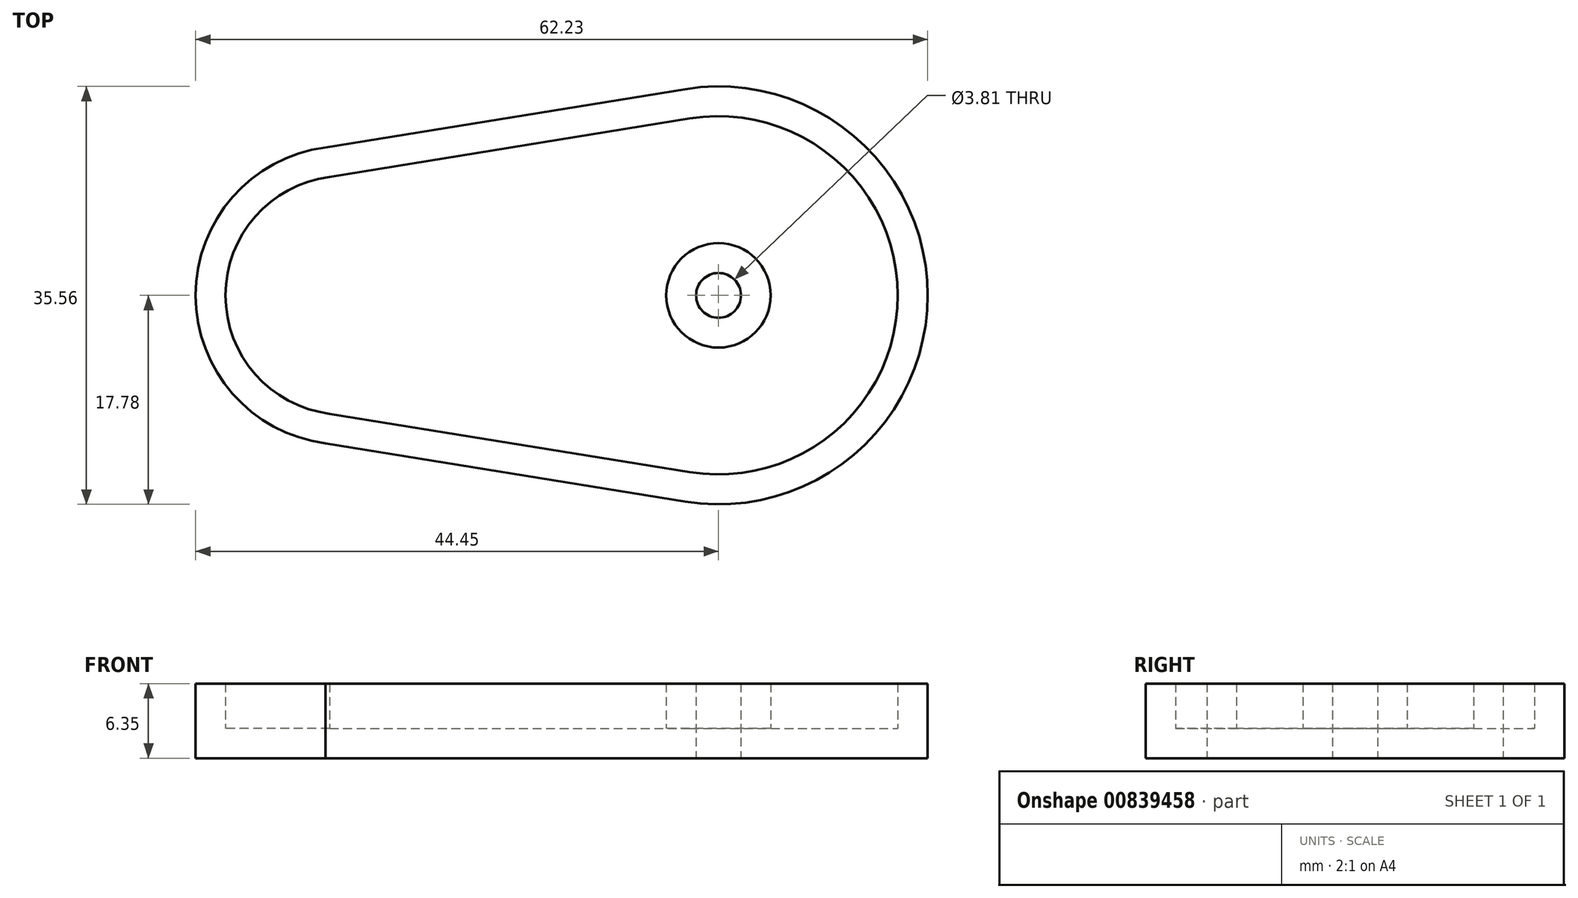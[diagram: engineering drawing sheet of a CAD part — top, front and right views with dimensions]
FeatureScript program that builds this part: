
annotation { "Feature Type Name" : "Feature", "Feature Type Description" : "" }
export const myFeature = defineFeature(function(context is Context, id is Id, definition is map)
    precondition{}
    {
        {
            var Q0;
            Q0=qCreatedBy(makeId("Top.planeOp"),FACE);
            var sketch = newSketch(context, id + "F0", { "sketchPlane" : qUnion([Q0])});
            skCircle(sketch, "E0", {"center": v(0, 0) * mm, "radius": 17.78 * mm});
            skCircle(sketch, "E1", {"center": v(-31.75, 0) * mm, "radius": 12.7 * mm});
            skLineSegment(sketch, "E2", {"start": v(-33.42, 12.59) * mm, "end": v(-2.85, 17.55) * mm});
            skLineSegment(sketch, "E3.MirrorCS", {"start": v(-33.42, -12.59) * mm, "end": v(-2.85, -17.55) * mm});
            skCircle(sketch, "E4", {"center": v(0, 0) * mm, "radius": 1.9 * mm});
            skSolve(sketch);
        }
        {
            var Q0;
            Q0 = qSketchRegion(id + "F0", true);
            extrude(context, id + "F1", {"entities" : qUnion([Q0]), "depth" : 6.35 * mm, "offsetDistance" : 25.4 * mm});
        }
        {
            var Q0;
            Q0=makeQuery(id+"F1.opExtrude","CAP_FACE",FACE,{"disambiguationData":[OSD([sQuery(id+"F0.wireOp",EDGE,"E0"),sQuery(id+"F0.wireOp",EDGE,"E1"),sQuery(id+"F0.wireOp",EDGE,"E2"),sQuery(id+"F0.wireOp",EDGE,"E3.MirrorCS"),sQuery(id+"F0.wireOp",EDGE,"E4")])],"isStart":false});
            shell(context, id + "F2", {"entities" : qUnion([Q0]), "thickness" : 2.54 * mm});
        }
    });
